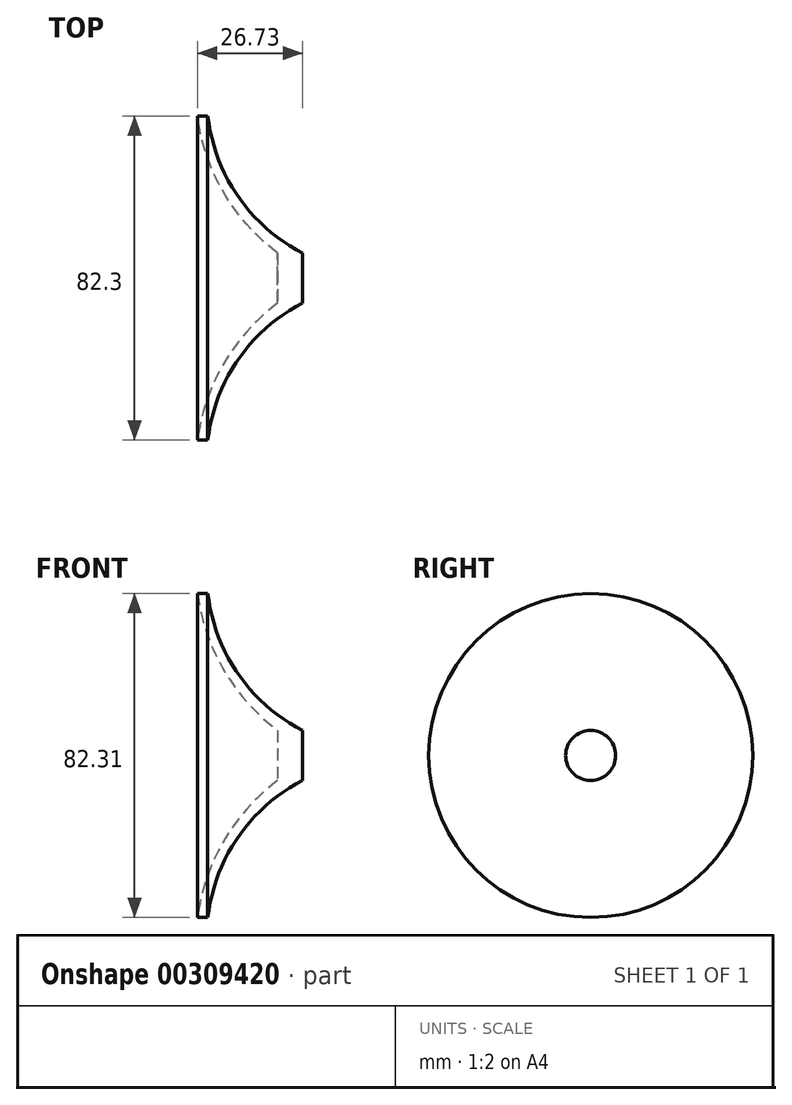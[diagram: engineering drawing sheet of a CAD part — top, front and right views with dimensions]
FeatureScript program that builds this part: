
annotation { "Feature Type Name" : "Feature", "Feature Type Description" : "" }
export const myFeature = defineFeature(function(context is Context, id is Id, definition is map)
    precondition{}
    {
        {
            var Q0;
            Q0=qCreatedBy(makeId("Front.planeOp"),FACE);
            var sketch = newSketch(context, id + "F0", { "sketchPlane" : qUnion([Q0])});
            skLineSegment(sketch, "E0", {"start": v(-35.96, -31.07) * mm, "end": v(-29.6, -31.07) * mm});
            skLineSegment(sketch, "E1", {"start": v(-35.96, -31.07) * mm, "end": v(-35.96, -24.72) * mm});
            skArc(sketch, "E2", {"start": v(-56.34, 10.09) * mm, "mid": v(-49.67, -9.37) * mm, "end": v(-35.96, -24.72) * mm});
            skLineSegment(sketch, "E3", {"start": v(-56.34, 10.09) * mm, "end": v(-53.74, 10.09) * mm});
            skLineSegment(sketch, "E4", {"start": v(-29.6, -31.07) * mm, "end": v(-29.6, -24.72) * mm});
            skArc(sketch, "E5", {"start": v(-53.74, 10.09) * mm, "mid": v(-46.03, -10.33) * mm, "end": v(-29.6, -24.72) * mm});
            skSolve(sketch);
        }
        {
            var Q0;
            Q0=makeQuery(id+"F0.imprint","IMPRINT",FACE,{"disambiguationData":[TD([[makeQuery(id+"F0.imprint","IMPRINT",EDGE,{"derivedFrom":sQuery(id+"F0.wireOp",EDGE,"E0")}),1.0]])]});
            var Q1;
            Q1=sQuery(id+"F0.wireOp",EDGE,"E0");
            revolve(context, id + "F1", {"entities" : qUnion([Q0]), "axis" : qUnion([Q1]), "revolveType" : RevolveType.FULL});
        }
        {
            var Q0;
            Q0=qCreatedBy(makeId("Right.planeOp"),FACE);
            var sketch = newSketch(context, id + "F2", { "sketchPlane" : qUnion([Q0])});
            skCircle(sketch, "E6", {"center": v(-2.14, -28.2) * mm, "radius": 6.37 * mm});
            skSolve(sketch);
        }
        {
            var Q0;
            Q0 = qSketchRegion(id + "F2", true);
            extrude(context, id + "F3", {"entities" : qUnion([Q0]), "operationType" : NewBodyOperationType.REMOVE, "oppositeDirection" : true, "depth" : 25.4 * mm});
        }
    });
